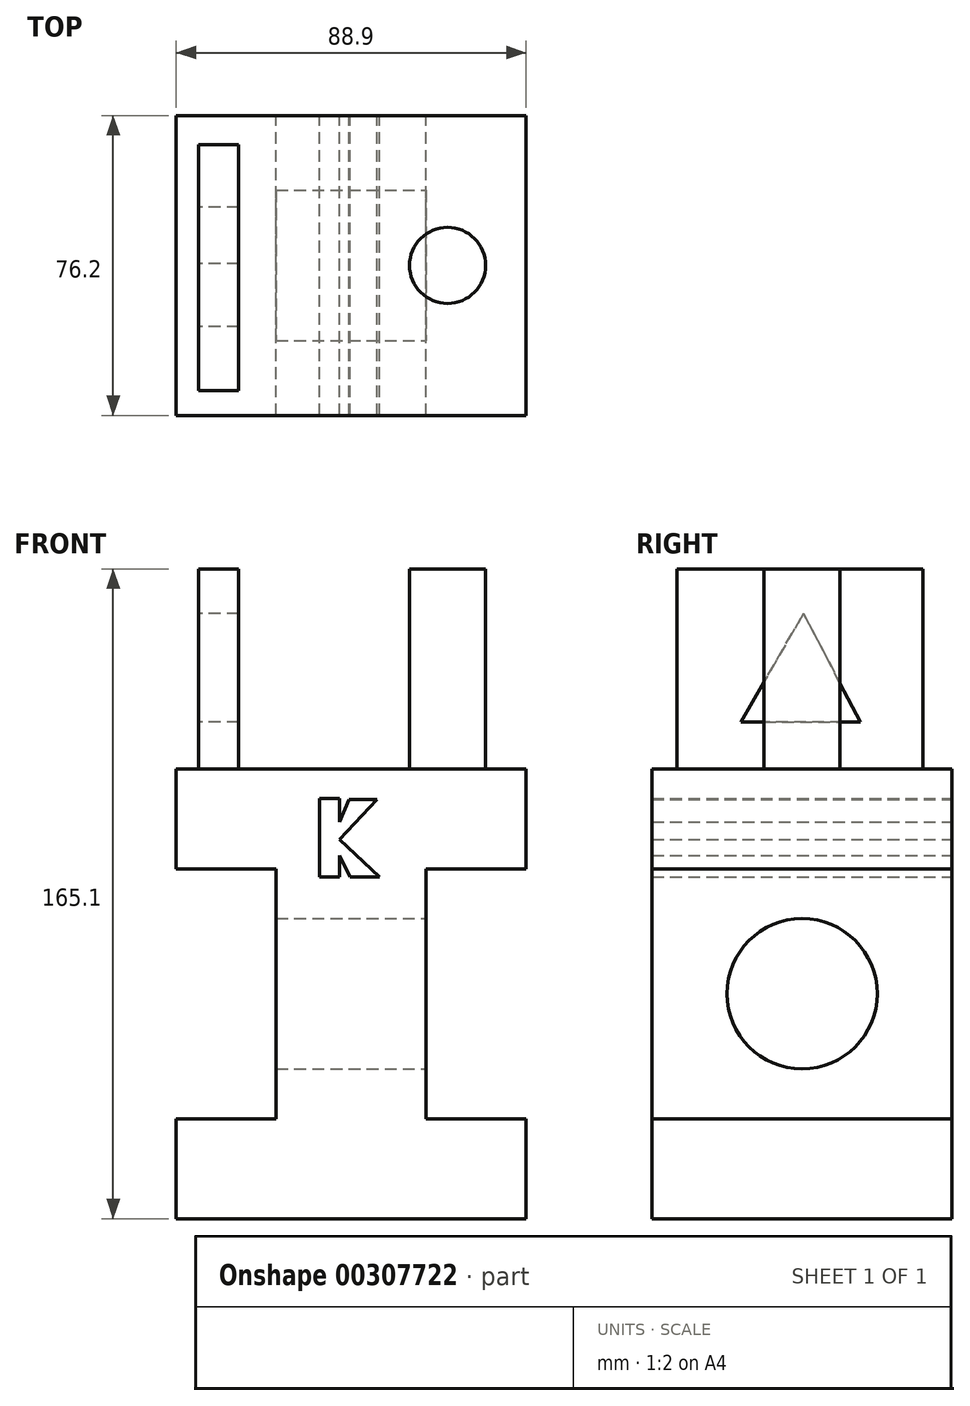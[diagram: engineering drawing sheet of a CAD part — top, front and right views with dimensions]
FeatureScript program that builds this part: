
annotation { "Feature Type Name" : "Feature", "Feature Type Description" : "" }
export const myFeature = defineFeature(function(context is Context, id is Id, definition is map)
    precondition{}
    {
        {
            var Q0;
            Q0=qCreatedBy(makeId("Front.planeOp"),FACE);
            var sketch = newSketch(context, id + "F0", { "sketchPlane" : qUnion([Q0])});
            skLineSegment(sketch, "E0", {"start": v(-43.91, -44.43) * mm, "end": v(44.99, -44.43) * mm});
            skLineSegment(sketch, "E1", {"start": v(44.99, -44.43) * mm, "end": v(44.99, -19.03) * mm});
            skLineSegment(sketch, "E2", {"start": v(44.99, -19.03) * mm, "end": v(19.59, -19.03) * mm});
            skLineSegment(sketch, "E3", {"start": v(19.59, -19.03) * mm, "end": v(19.59, 44.47) * mm});
            skLineSegment(sketch, "E4", {"start": v(19.59, 44.47) * mm, "end": v(44.99, 44.47) * mm});
            skLineSegment(sketch, "E5", {"start": v(44.99, 44.47) * mm, "end": v(44.99, 69.87) * mm});
            skLineSegment(sketch, "E6", {"start": v(44.99, 69.87) * mm, "end": v(-43.91, 69.87) * mm});
            skLineSegment(sketch, "E7", {"start": v(-43.91, 69.87) * mm, "end": v(-43.91, 44.47) * mm});
            skLineSegment(sketch, "E8", {"start": v(-43.91, 44.47) * mm, "end": v(-18.51, 44.47) * mm});
            skLineSegment(sketch, "E9", {"start": v(-18.51, 44.47) * mm, "end": v(-18.51, -19.03) * mm});
            skLineSegment(sketch, "E10", {"start": v(-18.51, -19.03) * mm, "end": v(-43.91, -19.03) * mm});
            skLineSegment(sketch, "E11", {"start": v(-43.91, -19.03) * mm, "end": v(-43.91, -44.43) * mm});
            skSolve(sketch);
        }
        {
            var Q0;
            Q0=makeQuery(id+"F0.imprint","IMPRINT",FACE,{"disambiguationData":[TD([[makeQuery(id+"F0.imprint","IMPRINT",EDGE,{"derivedFrom":sQuery(id+"F0.wireOp",EDGE,"E0")}),1.0]])]});
            extrude(context, id + "F1", {"entities" : qUnion([Q0]), "depth" : 76.2 * mm});
        }
        {
            var Q0;
            Q0=makeQuery(id+"F1.opExtrude","SWEPT_FACE",FACE,{"disambiguationData":[OSD([sQuery(id+"F0.wireOp",EDGE,"E3")])]});
            var sketch = newSketch(context, id + "F2", { "sketchPlane" : qUnion([Q0])});
            skCircle(sketch, "E12", {"center": v(-38.1, 12.72) * mm, "radius": 19.1 * mm});
            skPoint(sketch, "E12.centerSnap0", {"position": v(-38.1, 44.47) * mm});
            skPoint(sketch, "E12.centerSnap1", {"position": v(-76.2, 12.72) * mm});
            skSolve(sketch);
        }
        {
            var Q0;
            Q0=makeQuery(id+"F2.imprint","IMPRINT",FACE,{"disambiguationData":[TD([[makeQuery(id+"F2.imprint","IMPRINT",EDGE,{"derivedFrom":sQuery(id+"F2.wireOp",EDGE,"E12")}),1.0]])]});
            extrude(context, id + "F3", {"entities" : qUnion([Q0]), "operationType" : NewBodyOperationType.REMOVE, "oppositeDirection" : true, "depth" : 47.5 * mm});
        }
        {
            var Q0;
            Q0=makeQuery(id+"F1.opExtrude","SWEPT_FACE",FACE,{"disambiguationData":[OSD([sQuery(id+"F0.wireOp",EDGE,"E6")])]});
            var sketch = newSketch(context, id + "F4", { "sketchPlane" : qUnion([Q0])});
            skLineSegment(sketch, "E13.bottom", {"start": v(-38.21, -7.44) * mm, "end": v(-28.05, -7.44) * mm});
            skLineSegment(sketch, "E13.top", {"start": v(-38.21, -69.88) * mm, "end": v(-28.05, -69.88) * mm});
            skLineSegment(sketch, "E13.left", {"start": v(-38.21, -7.44) * mm, "end": v(-38.21, -69.88) * mm});
            skLineSegment(sketch, "E13.right", {"start": v(-28.05, -7.44) * mm, "end": v(-28.05, -69.88) * mm});
            skSolve(sketch);
        }
        {
            var Q0;
            Q0=makeQuery(id+"F4.imprint","IMPRINT",FACE,{"disambiguationData":[TD([[makeQuery(id+"F4.imprint","IMPRINT",EDGE,{"derivedFrom":sQuery(id+"F4.wireOp",EDGE,"E13.bottom")}),-1.0]])]});
            extrude(context, id + "F5", {"entities" : qUnion([Q0]), "operationType" : NewBodyOperationType.ADD, "depth" : 50.8 * mm});
        }
        {
            var Q0;
            Q0=makeQuery(id+"F5.opExtrude","SWEPT_FACE",FACE,{"disambiguationData":[OSD([sQuery(id+"F4.wireOp",EDGE,"E13.left")])]});
            var sketch = newSketch(context, id + "F6", { "sketchPlane" : qUnion([Q0])});
            skLineSegment(sketch, "E14", {"start": v(37.7, 109.32) * mm, "end": v(23.28, 81.72) * mm});
            skLineSegment(sketch, "E15", {"start": v(23.28, 81.72) * mm, "end": v(53.63, 81.72) * mm});
            skLineSegment(sketch, "E16", {"start": v(53.63, 81.72) * mm, "end": v(37.7, 109.32) * mm});
            skSolve(sketch);
        }
        {
            var Q0;
            Q0=makeQuery(id+"F6.imprint","IMPRINT",FACE,{"disambiguationData":[TD([[makeQuery(id+"F6.imprint","IMPRINT",EDGE,{"derivedFrom":sQuery(id+"F6.wireOp",EDGE,"E14")}),1.0]])]});
            extrude(context, id + "F7", {"entities" : qUnion([Q0]), "operationType" : NewBodyOperationType.REMOVE, "oppositeDirection" : true, "depth" : 25.4 * mm});
        }
        {
            var Q0;
            Q0=makeQuery(id+"F1.opExtrude","CAP_FACE",FACE,{"disambiguationData":[OSD([sQuery(id+"F0.wireOp",EDGE,"E0"),sQuery(id+"F0.wireOp",EDGE,"E1"),sQuery(id+"F0.wireOp",EDGE,"E2"),sQuery(id+"F0.wireOp",EDGE,"E3"),sQuery(id+"F0.wireOp",EDGE,"E4"),sQuery(id+"F0.wireOp",EDGE,"E5"),sQuery(id+"F0.wireOp",EDGE,"E6"),sQuery(id+"F0.wireOp",EDGE,"E7"),sQuery(id+"F0.wireOp",EDGE,"E8"),sQuery(id+"F0.wireOp",EDGE,"E9"),sQuery(id+"F0.wireOp",EDGE,"E10"),sQuery(id+"F0.wireOp",EDGE,"E11")])],"isStart":true});
            var sketch = newSketch(context, id + "F8", { "sketchPlane" : qUnion([Q0])});
            skLineSegment(sketch, "E17", {"start": v(7.51, 62.38) * mm, "end": v(7.51, 42.38) * mm});
            skLineSegment(sketch, "E18", {"start": v(7.51, 42.38) * mm, "end": v(2.47, 42.38) * mm});
            skLineSegment(sketch, "E19", {"start": v(2.47, 42.38) * mm, "end": v(2.47, 47.86) * mm});
            skLineSegment(sketch, "E20", {"start": v(2.47, 47.86) * mm, "end": v(-0.3, 42.38) * mm});
            skLineSegment(sketch, "E21", {"start": v(-0.3, 42.38) * mm, "end": v(-7.7, 42.38) * mm});
            skLineSegment(sketch, "E22", {"start": v(-7.7, 42.38) * mm, "end": v(2.47, 51.96) * mm});
            skLineSegment(sketch, "E23", {"start": v(2.47, 51.96) * mm, "end": v(-7.08, 62.1) * mm});
            skLineSegment(sketch, "E24", {"start": v(-7.08, 62.1) * mm, "end": v(0, 62.1) * mm});
            skLineSegment(sketch, "E25", {"start": v(0, 62.1) * mm, "end": v(2.47, 56.3) * mm});
            skLineSegment(sketch, "E26", {"start": v(2.47, 56.3) * mm, "end": v(2.47, 62.38) * mm});
            skLineSegment(sketch, "E27", {"start": v(2.47, 62.38) * mm, "end": v(7.51, 62.38) * mm});
            skSolve(sketch);
        }
        {
            var Q0;
            Q0=makeQuery(id+"F8.imprint","IMPRINT",FACE,{"disambiguationData":[TD([[makeQuery(id+"F8.imprint","IMPRINT",EDGE,{"derivedFrom":sQuery(id+"F8.wireOp",EDGE,"CcmsoerV-0mRk-mgOg-3ddJ-oTUTscYfJOUJ")}),1.0]])]});
            var Q1;
            Q1=makeQuery(id+"F8.imprint","IMPRINT",FACE,{"disambiguationData":[TD([[makeQuery(id+"F8.imprint","IMPRINT",EDGE,{"derivedFrom":sQuery(id+"F8.wireOp",EDGE,"E17")}),-1.0]])]});
            extrude(context, id + "F9", {"entities" : qUnion([Q0, Q1]), "operationType" : NewBodyOperationType.REMOVE, "oppositeDirection" : true, "depth" : 96.52 * mm});
        }
        {
            var Q0;
            Q0=makeQuery(id+"F1.opExtrude","SWEPT_FACE",FACE,{"disambiguationData":[OSD([sQuery(id+"F0.wireOp",EDGE,"E6")])]});
            var sketch = newSketch(context, id + "F10", { "sketchPlane" : qUnion([Q0])});
            skCircle(sketch, "E28", {"center": v(25.04, -38.1) * mm, "radius": 9.66 * mm});
            skPoint(sketch, "E28.centerSnap0", {"position": v(44.99, -38.1) * mm});
            skSolve(sketch);
        }
        {
            var Q0;
            Q0=makeQuery(id+"F10.imprint","IMPRINT",FACE,{"disambiguationData":[TD([[makeQuery(id+"F10.imprint","IMPRINT",EDGE,{"derivedFrom":sQuery(id+"F10.wireOp",EDGE,"E28")}),1.0]])]});
            extrude(context, id + "F11", {"entities" : qUnion([Q0]), "operationType" : NewBodyOperationType.ADD, "depth" : 50.8 * mm});
        }
    });
